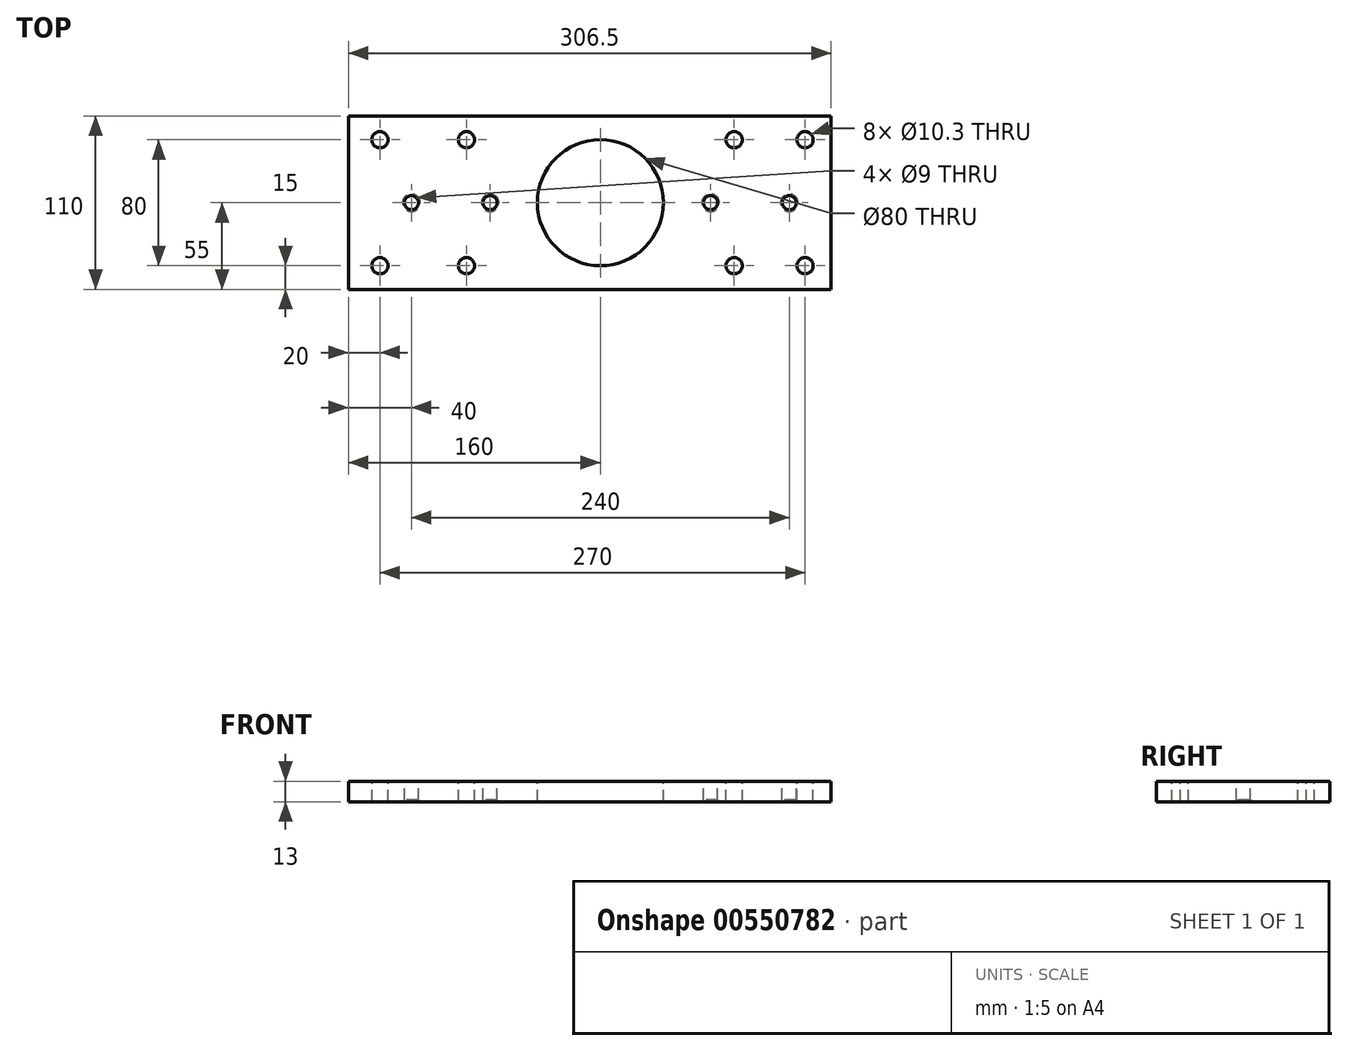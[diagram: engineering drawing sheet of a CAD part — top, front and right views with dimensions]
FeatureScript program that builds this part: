
annotation { "Feature Type Name" : "Feature", "Feature Type Description" : "" }
export const myFeature = defineFeature(function(context is Context, id is Id, definition is map)
    precondition{}
    {
        {
            var Q0;
            Q0=qCreatedBy(makeId("Top.planeOp"),FACE);
            var sketch = newSketch(context, id + "F0", { "sketchPlane" : qUnion([Q0])});
            skLineSegment(sketch, "E0.bottom", {"start": v(153.25, 55) * mm, "end": v(-153.25, 55) * mm});
            skLineSegment(sketch, "E0.top", {"start": v(153.25, -55) * mm, "end": v(-153.25, -55) * mm});
            skLineSegment(sketch, "E0.left", {"start": v(153.25, 55) * mm, "end": v(153.25, -55) * mm});
            skLineSegment(sketch, "E0.right", {"start": v(-153.25, 55) * mm, "end": v(-153.25, -55) * mm});
            skPoint(sketch, "E0.middle", {"position": v(0, 0) * mm});
            skPoint(sketch, "E1", {"position": v(-63.25, 0) * mm});
            skPoint(sketch, "E2", {"position": v(-113.25, 0) * mm});
            skPoint(sketch, "E3", {"position": v(76.75, 0) * mm});
            skPoint(sketch, "E4", {"position": v(126.75, 0) * mm});
            skPoint(sketch, "E5", {"position": v(-133.25, -40) * mm});
            skPoint(sketch, "E6", {"position": v(-78.25, -40) * mm});
            skPoint(sketch, "E7", {"position": v(91.75, -40) * mm});
            skPoint(sketch, "E8", {"position": v(136.75, -40) * mm});
            skPoint(sketch, "E9", {"position": v(136.75, 40) * mm});
            skPoint(sketch, "E10", {"position": v(91.75, 40) * mm});
            skPoint(sketch, "E11", {"position": v(-78.25, 40) * mm});
            skPoint(sketch, "E12", {"position": v(-133.25, 40) * mm});
            skPoint(sketch, "E13", {"position": v(6.75, 0) * mm});
            skSolve(sketch);
        }
        {
            var Q0;
            Q0=makeQuery(id+"F0.imprint","IMPRINT",FACE,{"disambiguationData":[TD([[makeQuery(id+"F0.imprint","IMPRINT",EDGE,{"derivedFrom":sQuery(id+"F0.wireOp",EDGE,"E0.bottom")}),1.0]])]});
            extrude(context, id + "F1", {"entities" : qUnion([Q0]), "depth" : 13 * mm, "offsetDistance" : 25 * mm});
        }
        {
            var Q0;
            Q0=sQuery(id+"F0.wireOp",VERTEX,"E2");
            var Q1;
            Q1=sQuery(id+"F0.wireOp",VERTEX,"E1");
            var Q2;
            Q2=sQuery(id+"F0.wireOp",VERTEX,"E3");
            var Q3;
            Q3=sQuery(id+"F0.wireOp",VERTEX,"E4");
            var Q4;
            Q4=makeQuery(id+"F1.opExtrude","SWEPT_BODY",BODY,{"disambiguationData":[OSD([sQuery(id+"F0.wireOp",EDGE,"E0.bottom"),sQuery(id+"F0.wireOp",EDGE,"E0.top"),sQuery(id+"F0.wireOp",EDGE,"E0.left"),sQuery(id+"F0.wireOp",EDGE,"E0.right")])]});
            hole(context, id + "F2", {"style" : HoleStyle.C_SINK, "endStyle" : HoleEndStyle.THROUGH, "oppositeDirection" : true, "standardTappedOrClearance" : lookupTablePath({ "standard" : "ISO", "size" : "9", "type" : "Drilled" }), "standardBlindInLast" : lookupTablePath({ "standard" : "ISO", "size" : "9", "type" : "Drilled" }), "holeDiameter" : 9 * mm, "cSinkDiameter" : 11.2 * mm, "cSinkAngle" : 90 * degree, "isTappedThrough" : true, "tappedDepth" : 3.5 * mm, "tapClearance" : 3, "locations" : qUnion([Q0, Q1, Q2, Q3]), "scope" : qUnion([Q4])});
        }
        {
            var Q0;
            Q0=sQuery(id+"F0.wireOp",VERTEX,"E13");
            var Q1;
            Q1=makeQuery(id+"F1.opExtrude","SWEPT_BODY",BODY,{"disambiguationData":[OSD([sQuery(id+"F0.wireOp",EDGE,"E0.bottom"),sQuery(id+"F0.wireOp",EDGE,"E0.top"),sQuery(id+"F0.wireOp",EDGE,"E0.left"),sQuery(id+"F0.wireOp",EDGE,"E0.right")])]});
            hole(context, id + "F3", {"style" : HoleStyle.SIMPLE, "endStyle" : HoleEndStyle.THROUGH, "oppositeDirection" : true, "holeDiameter" : 80 * mm, "isTappedThrough" : true, "tappedDepth" : 3.5 * mm, "tapClearance" : 3, "locations" : qUnion([Q0]), "scope" : qUnion([Q1])});
        }
        {
            var Q0;
            Q0=sQuery(id+"F0.wireOp",VERTEX,"E5");
            var Q1;
            Q1=sQuery(id+"F0.wireOp",VERTEX,"E6");
            var Q2;
            Q2=sQuery(id+"F0.wireOp",VERTEX,"E12");
            var Q3;
            Q3=sQuery(id+"F0.wireOp",VERTEX,"E11");
            var Q4;
            Q4=sQuery(id+"F0.wireOp",VERTEX,"E7");
            var Q5;
            Q5=sQuery(id+"F0.wireOp",VERTEX,"E8");
            var Q6;
            Q6=sQuery(id+"F0.wireOp",VERTEX,"E10");
            var Q7;
            Q7=sQuery(id+"F0.wireOp",VERTEX,"E9");
            var Q8;
            Q8=makeQuery(id+"F1.opExtrude","SWEPT_BODY",BODY,{"disambiguationData":[OSD([sQuery(id+"F0.wireOp",EDGE,"E0.bottom"),sQuery(id+"F0.wireOp",EDGE,"E0.top"),sQuery(id+"F0.wireOp",EDGE,"E0.left"),sQuery(id+"F0.wireOp",EDGE,"E0.right")])]});
            hole(context, id + "F4", {"style" : HoleStyle.SIMPLE, "endStyle" : HoleEndStyle.THROUGH, "oppositeDirection" : true, "standardTappedOrClearance" : lookupTablePath({ "standard" : "ISO", "engagement" : "75%", "pitch" : "1.75 mm", "size" : "M12", "type" : "Tapped" }), "standardBlindInLast" : lookupTablePath({ "standard" : "ISO", "engagement" : "75%", "pitch" : "1.75 mm", "size" : "M12", "type" : "Tapped" }), "holeDiameter" : 10.3 * mm, "showTappedDepth" : true, "isTappedThrough" : true, "tappedDepth" : 6.75 * mm, "tapClearance" : 3, "locations" : qUnion([Q0, Q1, Q2, Q3, Q4, Q5, Q6, Q7]), "scope" : qUnion([Q8]), "majorDiameter" : 12 * mm});
        }
    });
